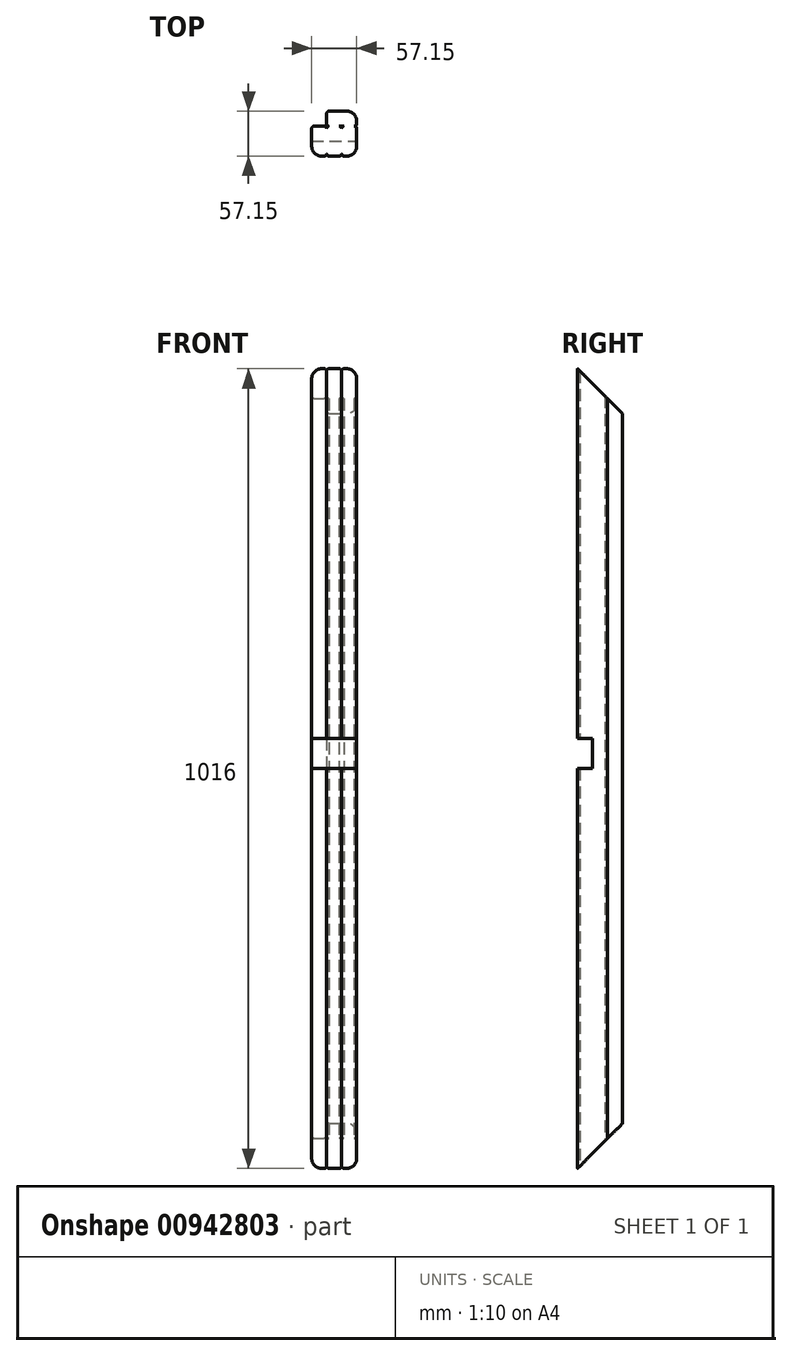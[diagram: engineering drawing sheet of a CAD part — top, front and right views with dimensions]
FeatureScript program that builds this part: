
annotation { "Feature Type Name" : "Feature", "Feature Type Description" : "" }
export const myFeature = defineFeature(function(context is Context, id is Id, definition is map)
    precondition{}
    {
        {
            var Q0;
            Q0=qCreatedBy(makeId("Top.planeOp"),FACE);
            var sketch = newSketch(context, id + "F0", { "sketchPlane" : qUnion([Q0])});
            skLineSegment(sketch, "E0.bottom", {"start": v(12.7, 0) * mm, "end": v(15.9, 0) * mm});
            skLineSegment(sketch, "E0.top", {"start": v(3.15, 38.1) * mm, "end": v(15.9, 38.1) * mm});
            skLineSegment(sketch, "E0.left", {"start": v(0, 12.7) * mm, "end": v(0, 34.95) * mm});
            skLineSegment(sketch, "E0.right", {"start": v(19.05, 3.15) * mm, "end": v(19.05, 34.95) * mm});
            skPoint(sketch, "E1.visualSharp", {"position": v(0, 38.1) * mm});
            skArc(sketch, "E1.filletArc", {"start": v(3.15, 38.1) * mm, "mid": v(0.92, 37.18) * mm, "end": v(0, 34.95) * mm});
            skPoint(sketch, "E2.visualSharp", {"position": v(19.05, 38.1) * mm});
            skArc(sketch, "E2.filletArc", {"start": v(19.05, 34.95) * mm, "mid": v(18.13, 37.18) * mm, "end": v(15.9, 38.1) * mm});
            skPoint(sketch, "E3.visualSharp", {"position": v(19.05, 0) * mm});
            skArc(sketch, "E3.filletArc", {"start": v(15.9, 0) * mm, "mid": v(18.13, 0.92) * mm, "end": v(19.05, 3.15) * mm});
            skPoint(sketch, "E4.visualSharp", {"position": v(0, 0) * mm});
            skArc(sketch, "E4.filletArc", {"start": v(0, 12.7) * mm, "mid": v(3.72, 3.72) * mm, "end": v(12.7, 0) * mm});
            skLineSegment(sketch, "E5.bottom", {"start": v(22.2, 0) * mm, "end": v(34.95, 0) * mm});
            skLineSegment(sketch, "E5.top", {"start": v(22.2, 38.1) * mm, "end": v(34.95, 38.1) * mm});
            skLineSegment(sketch, "E5.right", {"start": v(38.1, 3.15) * mm, "end": v(38.1, 34.95) * mm});
            skArc(sketch, "E6.filletArc", {"start": v(22.2, 38.1) * mm, "mid": v(19.97, 37.18) * mm, "end": v(19.05, 34.95) * mm});
            skPoint(sketch, "E7.visualSharp", {"position": v(38.1, 38.1) * mm});
            skArc(sketch, "E7.filletArc", {"start": v(38.1, 34.95) * mm, "mid": v(37.18, 37.18) * mm, "end": v(34.95, 38.1) * mm});
            skPoint(sketch, "E8.visualSharp", {"position": v(38.1, 0) * mm});
            skArc(sketch, "E8.filletArc", {"start": v(34.95, 0) * mm, "mid": v(37.18, 0.92) * mm, "end": v(38.1, 3.15) * mm});
            skArc(sketch, "E9.filletArc", {"start": v(19.05, 3.15) * mm, "mid": v(19.97, 0.92) * mm, "end": v(22.2, 0) * mm});
            skLineSegment(sketch, "E10.bottom", {"start": v(41.25, 0) * mm, "end": v(44.45, 0) * mm});
            skLineSegment(sketch, "E10.top", {"start": v(41.25, 38.1) * mm, "end": v(54, 38.1) * mm});
            skLineSegment(sketch, "E10.right", {"start": v(57.15, 12.7) * mm, "end": v(57.15, 34.95) * mm});
            skArc(sketch, "E11.filletArc", {"start": v(41.25, 38.1) * mm, "mid": v(39.02, 37.18) * mm, "end": v(38.1, 34.95) * mm});
            skPoint(sketch, "E12.visualSharp", {"position": v(57.15, 38.1) * mm});
            skArc(sketch, "E12.filletArc", {"start": v(57.15, 34.95) * mm, "mid": v(56.23, 37.18) * mm, "end": v(54, 38.1) * mm});
            skPoint(sketch, "E13.visualSharp", {"position": v(57.15, 0) * mm});
            skArc(sketch, "E13.filletArc", {"start": v(44.45, 0) * mm, "mid": v(53.43, 3.72) * mm, "end": v(57.15, 12.7) * mm});
            skArc(sketch, "E14.filletArc", {"start": v(38.1, 3.15) * mm, "mid": v(39.02, 0.92) * mm, "end": v(41.25, 0) * mm});
            skLineSegment(sketch, "E15.bottom", {"start": v(57.15, 41.25) * mm, "end": v(57.15, 44.45) * mm});
            skLineSegment(sketch, "E15.top", {"start": v(19.05, 41.25) * mm, "end": v(19.05, 54) * mm});
            skLineSegment(sketch, "E15.left", {"start": v(54, 38.1) * mm, "end": v(22.2, 38.1) * mm});
            skLineSegment(sketch, "E15.right", {"start": v(44.45, 57.15) * mm, "end": v(22.2, 57.15) * mm});
            skArc(sketch, "E16.filletArc", {"start": v(19.05, 41.25) * mm, "mid": v(19.97, 39.02) * mm, "end": v(22.2, 38.1) * mm});
            skPoint(sketch, "E17.visualSharp", {"position": v(19.05, 57.15) * mm});
            skArc(sketch, "E17.filletArc", {"start": v(22.2, 57.15) * mm, "mid": v(19.97, 56.23) * mm, "end": v(19.05, 54) * mm});
            skPoint(sketch, "E18.visualSharp", {"position": v(57.15, 57.15) * mm});
            skArc(sketch, "E18.filletArc", {"start": v(57.15, 44.45) * mm, "mid": v(53.43, 53.43) * mm, "end": v(44.45, 57.15) * mm});
            skArc(sketch, "E19.filletArc", {"start": v(54, 38.1) * mm, "mid": v(56.23, 39.02) * mm, "end": v(57.15, 41.25) * mm});
            skSolve(sketch);
        }
        {
            var Q0;
            Q0=makeQuery(id+"F0.imprint","IMPRINT",FACE,{"disambiguationData":[TD([[makeQuery(id+"F0.imprint","IMPRINT",EDGE,{"derivedFrom":sQuery(id+"F0.wireOp",EDGE,"E0.bottom")}),1.0]])]});
            var Q1;
            Q1=makeQuery(id+"F0.imprint","IMPRINT",FACE,{"disambiguationData":[TD([[makeQuery(id+"F0.imprint","IMPRINT",EDGE,{"derivedFrom":sQuery(id+"F0.wireOp",EDGE,"E5.bottom")}),1.0]])]});
            var Q2;
            Q2=makeQuery(id+"F0.imprint","IMPRINT",FACE,{"disambiguationData":[TD([[makeQuery(id+"F0.imprint","IMPRINT",EDGE,{"derivedFrom":sQuery(id+"F0.wireOp",EDGE,"E10.bottom")}),1.0]])]});
            var Q3;
            Q3=makeQuery(id+"F0.imprint","IMPRINT",FACE,{"disambiguationData":[TD([[makeQuery(id+"F0.imprint","IMPRINT",EDGE,{"derivedFrom":sQuery(id+"F0.wireOp",EDGE,"E15.bottom")}),1.0]])]});
            extrude(context, id + "F1", {"entities" : qUnion([Q0, Q1, Q2, Q3]), "depth" : 1016 * mm, "offsetDistance" : 25.4 * mm});
        }
        {
            var Q0;
            Q0=makeQuery(id+"F1.opExtrude","SWEPT_FACE",FACE,{"disambiguationData":[OSD([sQuery(id+"F0.wireOp",EDGE,"E10.right")])]});
            var sketch = newSketch(context, id + "F2", { "sketchPlane" : qUnion([Q0])});
            skLineSegment(sketch, "E20.0", {"start": v(0, 1016) * mm, "end": v(12.7, 1016) * mm});
            skLineSegment(sketch, "E21.0", {"start": v(57.15, 1016) * mm, "end": v(57.15, 0) * mm});
            skLineSegment(sketch, "E22.0", {"start": v(0, 0) * mm, "end": v(12.7, 0) * mm});
            skLineSegment(sketch, "E23", {"start": v(0, 1016) * mm, "end": v(57.15, 1016) * mm});
            skLineSegment(sketch, "E24", {"start": v(57.15, 1016) * mm, "end": v(57.15, 958.85) * mm});
            skLineSegment(sketch, "E25", {"start": v(57.15, 958.85) * mm, "end": v(0, 1016) * mm});
            skLineSegment(sketch, "E26", {"start": v(0, 0) * mm, "end": v(57.15, 0) * mm});
            skLineSegment(sketch, "E27", {"start": v(57.15, 0) * mm, "end": v(57.15, 57.15) * mm});
            skLineSegment(sketch, "E28", {"start": v(57.15, 57.15) * mm, "end": v(0, 0) * mm});
            skLineSegment(sketch, "E29", {"start": v(57.15, 57.15) * mm, "end": v(57.15, 0) * mm});
            skSolve(sketch);
        }
        {
            var Q0;
            Q0=qSketchRegion(id+"F2",true);
            extrude(context, id + "F3", {"entities" : qUnion([Q0]), "operationType" : NewBodyOperationType.REMOVE, "endBound" : BoundingType.THROUGH_ALL, "oppositeDirection" : true, "depth" : 25.4 * mm, "offsetDistance" : 25.4 * mm});
        }
        {
            var Q0;
            Q0=makeQuery(id+"F1.opExtrude","SWEPT_FACE",FACE,{"disambiguationData":[OSD([sQuery(id+"F0.wireOp",EDGE,"E10.right")])]});
            var sketch = newSketch(context, id + "F4", { "sketchPlane" : qUnion([Q0])});
            skLineSegment(sketch, "E30.bottom", {"start": v(0, 508) * mm, "end": v(19.05, 508) * mm});
            skLineSegment(sketch, "E30.top", {"start": v(0, 546.1) * mm, "end": v(19.05, 546.1) * mm});
            skLineSegment(sketch, "E30.left", {"start": v(0, 508) * mm, "end": v(0, 546.1) * mm});
            skLineSegment(sketch, "E30.right", {"start": v(19.05, 508) * mm, "end": v(19.05, 546.1) * mm});
            skSolve(sketch);
        }
        {
            var Q0;
            Q0 = qSketchRegion(id + "F4", true);
            extrude(context, id + "F5", {"entities" : qUnion([Q0]), "operationType" : NewBodyOperationType.REMOVE, "endBound" : BoundingType.THROUGH_ALL, "oppositeDirection" : true, "depth" : 25.4 * mm, "offsetDistance" : 25.4 * mm});
        }
    });
